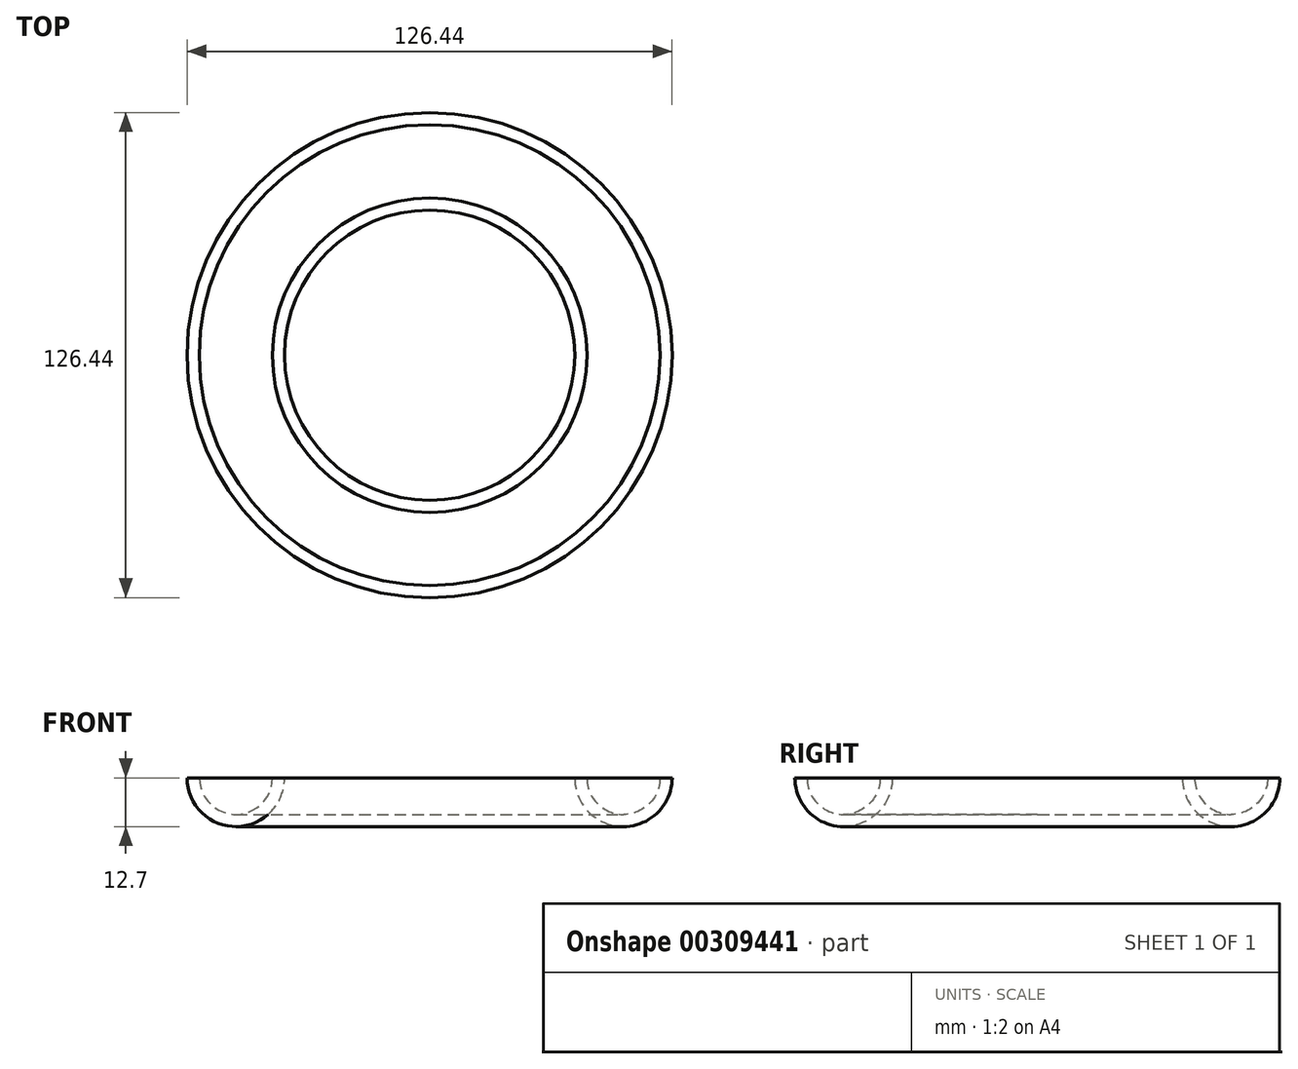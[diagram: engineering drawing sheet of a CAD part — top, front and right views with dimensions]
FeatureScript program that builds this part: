
annotation { "Feature Type Name" : "Feature", "Feature Type Description" : "" }
export const myFeature = defineFeature(function(context is Context, id is Id, definition is map)
    precondition{}
    {
        {
            var Q0;
            Q0=qCreatedBy(makeId("Front.planeOp"),FACE);
            var sketch = newSketch(context, id + "F0", { "sketchPlane" : qUnion([Q0])});
            skArc(sketch, "E0", {"start": v(37.82, 17.77) * mm, "mid": v(50.52, 5.07) * mm, "end": v(63.22, 17.77) * mm});
            skArc(sketch, "E1", {"start": v(41, 17.77) * mm, "mid": v(50.52, 8.24) * mm, "end": v(60.05, 17.77) * mm});
            skArc(sketch, "E2", {"start": v(-77.05, -29.1) * mm, "mid": v(-64.35, -41.8) * mm, "end": v(-51.65, -29.1) * mm});
            skArc(sketch, "E3", {"start": v(-73.88, -29.1) * mm, "mid": v(-64.35, -38.63) * mm, "end": v(-54.83, -29.1) * mm});
            skLineSegment(sketch, "E4", {"start": v(-51.65, -29.1) * mm, "end": v(-77.05, -29.1) * mm});
            skLineSegment(sketch, "E5", {"start": v(63.22, 17.77) * mm, "end": v(37.82, 17.77) * mm});
            skPoint(sketch, "E6.start.orphan", {"position": v(0, -54.27) * mm});
            skLineSegment(sketch, "E7", {"start": v(0, 0) * mm, "end": v(0, 40.63) * mm, "construction": true});
            skSolve(sketch);
        }
        {
            var Q0;
            {var subQ0=sQuery(id+"F0.wireOp",EDGE,"E0");Q0=makeQuery(id+"F0.imprint","IMPRINT",FACE,{"disambiguationData":[TD([[makeQuery(id+"F0.imprint","IMPRINT",EDGE,{"derivedFrom":subQ0}),1.0]])]});}
            var Q1;
            Q1=sQuery(id+"F0.wireOp",EDGE,"E7");
            revolve(context, id + "F1", {"entities" : qUnion([Q0]), "axis" : qUnion([Q1]), "revolveType" : RevolveType.FULL});
        }
    });
